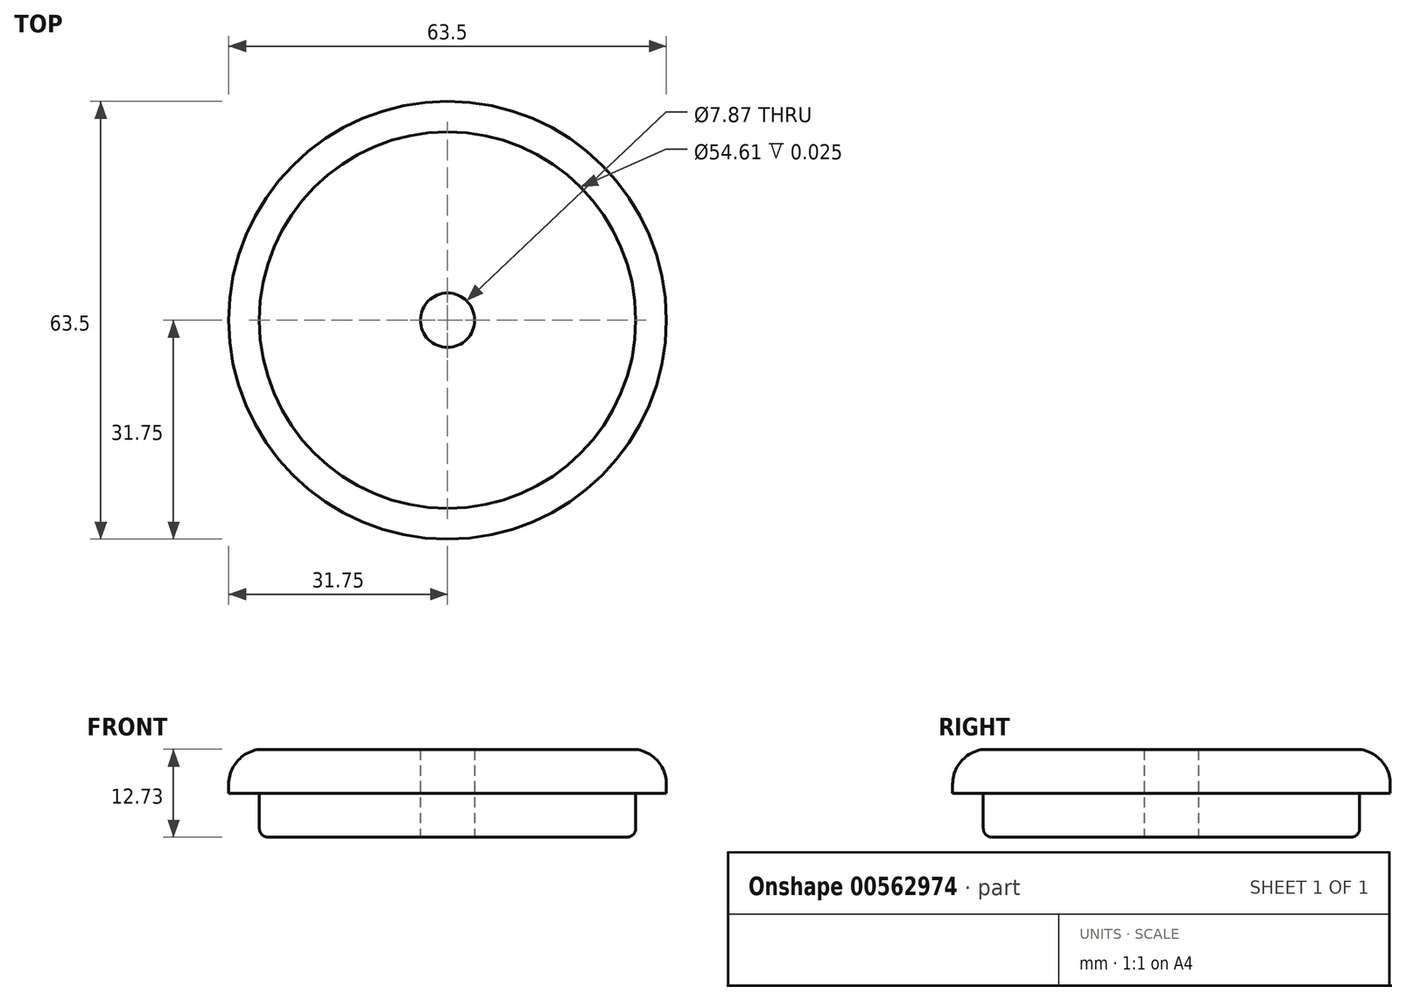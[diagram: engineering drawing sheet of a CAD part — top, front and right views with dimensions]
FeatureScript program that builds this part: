
annotation { "Feature Type Name" : "Feature", "Feature Type Description" : "" }
export const myFeature = defineFeature(function(context is Context, id is Id, definition is map)
    precondition{}
    {
        {
            var Q0;
            Q0=qCreatedBy(makeId("Top.planeOp"),FACE);
            var sketch = newSketch(context, id + "F0", { "sketchPlane" : qUnion([Q0])});
            skCircle(sketch, "E0", {"center": v(0, 0) * mm, "radius": 27.3 * mm});
            skCircle(sketch, "E1", {"center": v(0, 0) * mm, "radius": 31.75 * mm});
            skSolve(sketch);
        }
        {
            var Q0;
            Q0=makeQuery(id+"F0.imprint","IMPRINT",FACE,{"disambiguationData":[TD([[makeQuery(id+"F0.imprint","IMPRINT",EDGE,{"derivedFrom":sQuery(id+"F0.wireOp",EDGE,"E0")}),1.0]])]});
            extrude(context, id + "F1", {"entities" : qUnion([Q0]), "endBound" : BoundingType.SYMMETRIC, "depth" : 12.7 * mm, "offsetDistance" : 25.4 * mm});
        }
        {
            var Q0;
            Q0=qCreatedBy(makeId("Top.planeOp"),FACE);
            var sketch = newSketch(context, id + "F2", { "sketchPlane" : qUnion([Q0])});
            skCircle(sketch, "E2", {"center": v(0, 0) * mm, "radius": 3.94 * mm});
            skSolve(sketch);
        }
        {
            var Q0;
            Q0 = qSketchRegion(id + "F2", true);
            extrude(context, id + "F3", {"entities" : qUnion([Q0]), "operationType" : NewBodyOperationType.REMOVE, "endBound" : BoundingType.SYMMETRIC, "depth" : 25.4 * mm, "offsetDistance" : 25.4 * mm});
        }
        {
            var Q0;
            Q0=makeQuery(id+"F0.imprint","IMPRINT",FACE,{"disambiguationData":[TD([[makeQuery(id+"F0.imprint","IMPRINT",EDGE,{"derivedFrom":sQuery(id+"F0.wireOp",EDGE,"E0")}),-1.0]])]});
            extrude(context, id + "F4", {"entities" : qUnion([Q0]), "operationType" : NewBodyOperationType.ADD, "depth" : 6.38 * mm, "offsetDistance" : 25.4 * mm});
        }
        {
            var Q0;
            Q0=makeQuery(id+"F1.opExtrude","CAP_EDGE",EDGE,{"disambiguationData":[OSD([sQuery(id+"F0.wireOp",EDGE,"E0")])],"isStart":true});
            fillet(context, id + "F5", {"entities" : qUnion([Q0]), "radius" : 1.27 * mm, "tangentPropagation" : true, "allowEdgeOverflow" : false});
        }
        {
            var Q0;
            Q0=makeQuery(id+"F4.opExtrude","CAP_EDGE",EDGE,{"disambiguationData":[OSD([sQuery(id+"F0.wireOp",EDGE,"E1")])],"isStart":false});
            fillet(context, id + "F6", {"entities" : qUnion([Q0]), "radius" : 5.08 * mm, "tangentPropagation" : true, "allowEdgeOverflow" : false});
        }
    });
